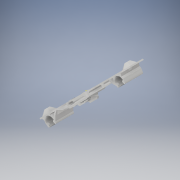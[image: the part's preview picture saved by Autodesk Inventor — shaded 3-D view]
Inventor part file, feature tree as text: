
AUTODESK INVENTOR PART (.ipt)
format: ipt  version: 2017 (Build 210142000, 142)  size: 1,233,408 bytes
history: native  units: in
note: dims shown in document units (in); Inventor stores cm internally (conversion verified against a paired STEP export)
features: sketch x5, extrude x3, other x2, projected_geometry x2, plane x1
ambient origin geometry x8: Origin, YZ Plane, XZ Plane, XY Plane, X Axis, Y Axis, Z Axis, Center Point
bodies: Solid1 (feature_tree)
feature tree (13):
  other  "10_Support plateau.STEP"
  plane  "Work Plane1"
  extrude  "Extrusion1"  Depth=0.3937in TaperAngle=0.0deg
  sketch  "Sketch2"  dims[d3=0.3937in d4=0.0in d5=0.3937in d6=0.0in]
  extrude  "Extrusion2"  Depth=0.3937in TaperAngle=0.0deg
  sketch  "Sketch4"
  extrude  "Extrusion3"  [1 undecoded]
  sketch  "Sketch1"  dims[d0=0.0in d1=0.3937in d2=0.0in]
  projected_geometry  "Projected Loop1"
  projected_geometry  "Projected Loop2"
  sketch  "Sketch3"
  sketch  "Sketch5"
  parser-record x1  (decoder bookkeeping rows leaked as tree rows — omitted from the tree; the rows remain in map.json)
note: 1 required parameter value undecoded (feature->parameter linkage not recoverable at this tier; creation-order binding heuristic only, values carry confidence <= 0.55)
